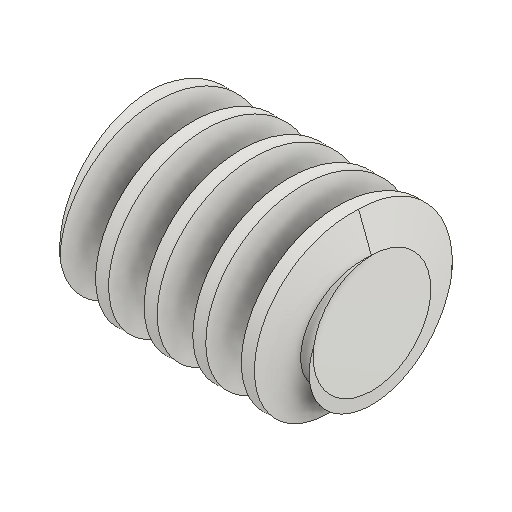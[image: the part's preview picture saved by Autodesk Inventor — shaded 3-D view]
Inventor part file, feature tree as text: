
AUTODESK INVENTOR PART (.ipt)
format: ipt  version: 2024.1 (Build 281209000, 209)  size: 286,720 bytes
history: native  units: mm (DEFAULTED — no unit token found)
features: other x6, chamfer x2, pattern_circular x2, extrude x1
ambient origin geometry x6: Origin, XZ Plane, X Axis, Y Axis, Z Axis, Center Point
bodies: Solid1 (feature_tree)
feature tree (11):
  extrude  "Grundkörper"  Depth=40.0mm
  chamfer  "Chamfer1"  Distance=48.0mm
  chamfer  "Chamfer2"  Distance=60.0mm
  other  "Zahnskizze"
  other  "Zahn"
  pattern_circular  "Zahnanordnung"  [2 undecoded]
  other  "Linker Zahn"
  pattern_circular  "Linke Zahnanordnung"  [2 undecoded]
  other  "Grundkörperskizze"
  other  "Srf1"
  other  "Flankendurchmesser"
note: 4 required parameter values undecoded (feature->parameter linkage not recoverable at this tier; creation-order binding heuristic only, values carry confidence <= 0.55)
